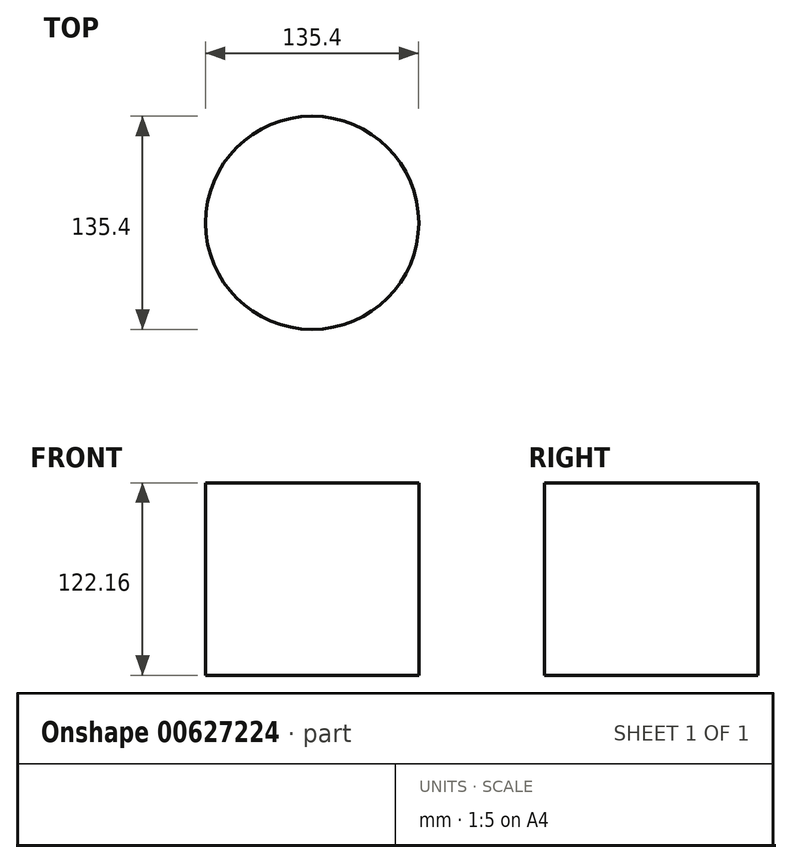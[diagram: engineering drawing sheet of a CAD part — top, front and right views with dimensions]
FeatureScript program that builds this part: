
annotation { "Feature Type Name" : "Feature", "Feature Type Description" : "" }
export const myFeature = defineFeature(function(context is Context, id is Id, definition is map)
    precondition{}
    {
        {
            var Q0;
            Q0=qCreatedBy(makeId("Top.planeOp"),FACE);
            var sketch = newSketch(context, id + "F0", { "sketchPlane" : qUnion([Q0])});
            skCircle(sketch, "E0", {"center": v(0, 0) * mm, "radius": 67.7 * mm});
            skSolve(sketch);
        }
        {
            var Q0;
            Q0=makeQuery(id+"F0.imprint","IMPRINT",FACE,{"disambiguationData":[TD([[makeQuery(id+"F0.imprint","IMPRINT",EDGE,{"derivedFrom":sQuery(id+"F0.wireOp",EDGE,"E0")}),1.0]])]});
            var Q1;
            Q1 = qSketchRegion(id + "F0", true);
            extrude(context, id + "F1", {"entities" : qUnion([Q0, Q1]), "depth" : 122.16 * mm, "offsetDistance" : 25.4 * mm});
        }
    });
